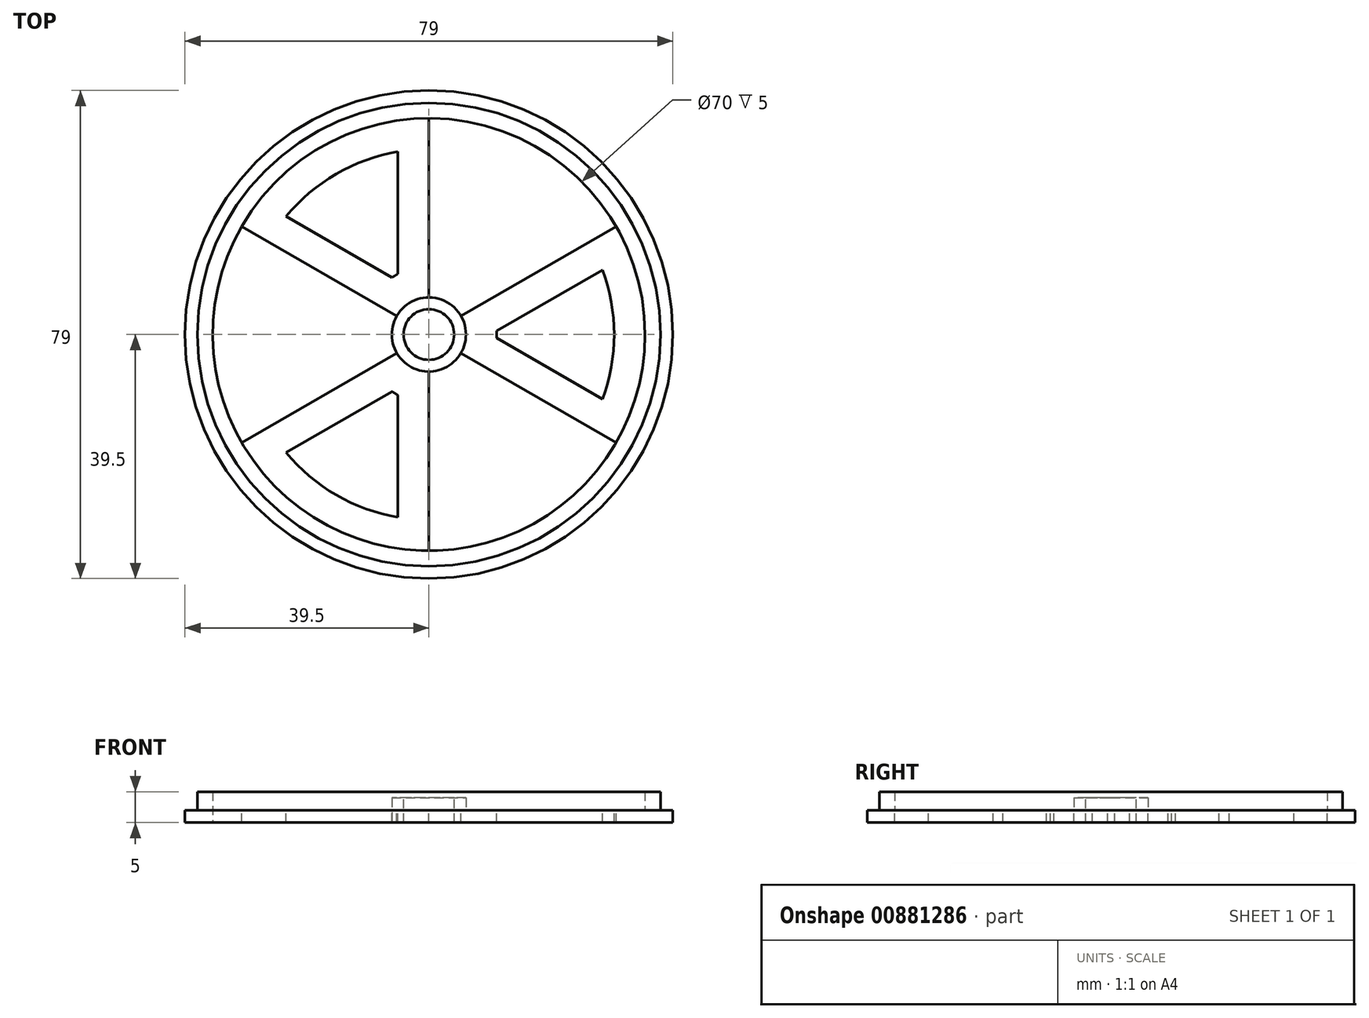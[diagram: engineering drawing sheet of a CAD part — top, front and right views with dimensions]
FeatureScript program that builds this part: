
annotation { "Feature Type Name" : "Feature", "Feature Type Description" : "" }
export const myFeature = defineFeature(function(context is Context, id is Id, definition is map)
    precondition{}
    {
        {
            var Q0;
            Q0=qCreatedBy(makeId("Top.planeOp"),FACE);
            var sketch = newSketch(context, id + "F0", { "sketchPlane" : qUnion([Q0])});
            skCircle(sketch, "E0", {"center": v(0, 0) * mm, "radius": 39.5 * mm});
            skSolve(sketch);
        }
        {
            var Q0;
            Q0=makeQuery(id+"F0.imprint","IMPRINT",FACE,{"disambiguationData":[TD([[makeQuery(id+"F0.imprint","IMPRINT",EDGE,{"derivedFrom":sQuery(id+"F0.wireOp",EDGE,"E0")}),1.0]])]});
            extrude(context, id + "F1", {"entities" : qUnion([Q0]), "depth" : 2 * mm, "offsetDistance" : 25 * mm});
        }
        {
            var Q0;
            Q0=makeQuery(id+"F1.opExtrude","CAP_FACE",FACE,{"disambiguationData":[OSD([sQuery(id+"F0.wireOp",EDGE,"E0")])],"isStart":false});
            var sketch = newSketch(context, id + "F2", { "sketchPlane" : qUnion([Q0])});
            skCircle(sketch, "E1", {"center": v(0, 0) * mm, "radius": 37.5 * mm});
            skCircle(sketch, "E2", {"center": v(0, 0) * mm, "radius": 35 * mm});
            skSolve(sketch);
        }
        {
            var Q0;
            Q0=makeQuery(id+"F2.imprint","IMPRINT",FACE,{"disambiguationData":[TD([[makeQuery(id+"F2.imprint","IMPRINT",EDGE,{"derivedFrom":sQuery(id+"F2.wireOp",EDGE,"E1")}),1.0]])]});
            extrude(context, id + "F3", {"entities" : qUnion([Q0]), "operationType" : NewBodyOperationType.ADD, "depth" : 3 * mm, "offsetDistance" : 25 * mm});
        }
        {
            var Q0;
            Q0=makeQuery(id+"F3.boolean.opBoolean","SPLIT",FACE,{"disambiguationData":[TD([makeQuery(id+"F3.opExtrude","SWEPT_FACE",FACE,{"disambiguationData":[OSD([sQuery(id+"F2.wireOp",EDGE,"E2")])]})])],"derivedFrom":makeQuery(id+"F1.opExtrude","CAP_FACE",FACE,{"disambiguationData":[OSD([sQuery(id+"F0.wireOp",EDGE,"E0")])],"isStart":false})});
            var sketch = newSketch(context, id + "F4", { "sketchPlane" : qUnion([Q0])});
            skCircle(sketch, "E3", {"center": v(0, 0) * mm, "radius": 4.1 * mm});
            skSolve(sketch);
        }
        {
            var Q0;
            Q0=makeQuery(id+"F4.imprint","IMPRINT",FACE,{"disambiguationData":[TD([[makeQuery(id+"F4.imprint","IMPRINT",EDGE,{"derivedFrom":sQuery(id+"F4.wireOp",EDGE,"E3")}),1.0]])]});
            extrude(context, id + "F5", {"entities" : qUnion([Q0]), "operationType" : NewBodyOperationType.REMOVE, "oppositeDirection" : true, "depth" : 25 * mm, "offsetDistance" : 25 * mm});
        }
        {
            var Q0;
            Q0=makeQuery(id+"F3.boolean.opBoolean","SPLIT",FACE,{"disambiguationData":[TD([makeQuery(id+"F3.opExtrude","SWEPT_FACE",FACE,{"disambiguationData":[OSD([sQuery(id+"F2.wireOp",EDGE,"E2")])]})])],"derivedFrom":makeQuery(id+"F1.opExtrude","CAP_FACE",FACE,{"disambiguationData":[OSD([sQuery(id+"F0.wireOp",EDGE,"E0")])],"isStart":false})});
            var sketch = newSketch(context, id + "F6", { "sketchPlane" : qUnion([Q0])});
            skCircle(sketch, "E4", {"center": v(0, 0) * mm, "radius": 4.1 * mm});
            skCircle(sketch, "E5", {"center": v(0, 0) * mm, "radius": 6 * mm});
            skSolve(sketch);
        }
        {
            var Q0;
            Q0=makeQuery(id+"F6.imprint","IMPRINT",FACE,{"disambiguationData":[TD([[makeQuery(id+"F6.imprint","IMPRINT",EDGE,{"derivedFrom":sQuery(id+"F6.wireOp",EDGE,"E4")}),-1.0]])]});
            extrude(context, id + "F7", {"entities" : qUnion([Q0]), "operationType" : NewBodyOperationType.ADD, "depth" : 2 * mm, "offsetDistance" : 25 * mm});
        }
        {
            var Q0;
            Q0=makeQuery(id+"F3.boolean.opBoolean","SPLIT",FACE,{"disambiguationData":[TD([makeQuery(id+"F3.opExtrude","SWEPT_FACE",FACE,{"disambiguationData":[OSD([sQuery(id+"F2.wireOp",EDGE,"E2")])]})])],"derivedFrom":makeQuery(id+"F1.opExtrude","CAP_FACE",FACE,{"disambiguationData":[OSD([sQuery(id+"F0.wireOp",EDGE,"E0")])],"isStart":false})});
            var sketch = newSketch(context, id + "F8", { "sketchPlane" : qUnion([Q0])});
            skCircle(sketch, "E6.cCircle", {"center": v(0, 0) * mm, "radius": 35 * mm, "construction": true});
            skLineSegment(sketch, "E6.0", {"start": v(0, 35) * mm, "end": v(30.31, 17.5) * mm});
            skLineSegment(sketch, "E6.1", {"start": v(30.31, 17.5) * mm, "end": v(30.31, -17.5) * mm});
            skLineSegment(sketch, "E6.2", {"start": v(30.31, -17.5) * mm, "end": v(0, -35) * mm});
            skLineSegment(sketch, "E6.3", {"start": v(0, -35) * mm, "end": v(-30.31, -17.5) * mm});
            skLineSegment(sketch, "E6.4", {"start": v(-30.31, -17.5) * mm, "end": v(-30.31, 17.5) * mm});
            skLineSegment(sketch, "E6.5", {"start": v(-30.31, 17.5) * mm, "end": v(0, 35) * mm});
            skCircle(sketch, "E7.cCircle", {"center": v(0, 0) * mm, "radius": 6 * mm, "construction": true});
            skLineSegment(sketch, "E7.0", {"start": v(0, 6) * mm, "end": v(5.2, 3) * mm});
            skLineSegment(sketch, "E7.1", {"start": v(5.2, 3) * mm, "end": v(5.2, -3) * mm});
            skLineSegment(sketch, "E7.2", {"start": v(5.2, -3) * mm, "end": v(0, -6) * mm});
            skLineSegment(sketch, "E7.3", {"start": v(0, -6) * mm, "end": v(-5.2, -3) * mm});
            skLineSegment(sketch, "E7.4", {"start": v(-5.2, -3) * mm, "end": v(-5.2, 3) * mm});
            skLineSegment(sketch, "E7.5", {"start": v(-5.2, 3) * mm, "end": v(0, 6) * mm});
            skLineSegment(sketch, "E8", {"start": v(0, 35) * mm, "end": v(0, 6) * mm});
            skLineSegment(sketch, "E9", {"start": v(30.31, 17.5) * mm, "end": v(5.2, 3) * mm});
            skLineSegment(sketch, "E10", {"start": v(30.31, -17.5) * mm, "end": v(5.2, -3) * mm});
            skLineSegment(sketch, "E11", {"start": v(0, -35) * mm, "end": v(0, -6) * mm});
            skLineSegment(sketch, "E12", {"start": v(-30.31, -17.5) * mm, "end": v(-5.2, -3) * mm});
            skLineSegment(sketch, "E13", {"start": v(-30.31, 17.5) * mm, "end": v(-5.2, 3) * mm});
            skSolve(sketch);
        }
        {
            var Q0;
            Q0=makeQuery(id+"F8.imprint","IMPRINT",FACE,{"disambiguationData":[TD([[makeQuery(id+"F8.imprint","IMPRINT",EDGE,{"derivedFrom":sQuery(id+"F8.wireOp",EDGE,"E6.0")}),-1.0]])]});
            var Q1;
            Q1=makeQuery(id+"F8.imprint","IMPRINT",FACE,{"disambiguationData":[TD([[makeQuery(id+"F8.imprint","IMPRINT",EDGE,{"derivedFrom":sQuery(id+"F8.wireOp",EDGE,"E6.2")}),-1.0]])]});
            var Q2;
            {var subQ0=sQuery(id+"F8.wireOp",EDGE,"E6.0");Q2=makeQuery(id+"F8.imprint","IMPRINT",FACE,{"disambiguationData":[TD([[makeQuery(id+"F8.imprint","IMPRINT",EDGE,{"derivedFrom":subQ0}),1.0]])]});}
            var Q3;
            {var subQ0=sQuery(id+"F8.wireOp",EDGE,"E6.2");Q3=makeQuery(id+"F8.imprint","IMPRINT",FACE,{"disambiguationData":[TD([[makeQuery(id+"F8.imprint","IMPRINT",EDGE,{"derivedFrom":subQ0}),1.0]])]});}
            var Q4;
            Q4=makeQuery(id+"F8.imprint","IMPRINT",FACE,{"disambiguationData":[TD([[makeQuery(id+"F8.imprint","IMPRINT",EDGE,{"derivedFrom":sQuery(id+"F8.wireOp",EDGE,"E6.4")}),-1.0]])]});
            var Q5;
            {var subQ0=sQuery(id+"F8.wireOp",EDGE,"E6.4");Q5=makeQuery(id+"F8.imprint","IMPRINT",FACE,{"disambiguationData":[TD([[makeQuery(id+"F8.imprint","IMPRINT",EDGE,{"derivedFrom":subQ0}),1.0]])]});}
            extrude(context, id + "F9", {"entities" : qUnion([Q0, Q1, Q2, Q3, Q4, Q5]), "operationType" : NewBodyOperationType.REMOVE, "oppositeDirection" : true, "depth" : 25 * mm, "offsetDistance" : 25 * mm});
        }
        {
            var Q0;
            {var subQ0=sQuery(id+"F8.wireOp",EDGE,"E9");var subQ4=sQuery(id+"F2.wireOp",EDGE,"E2");var subQ15=makeQuery(id+"F3.opExtrude","SWEPT_FACE",FACE,{"disambiguationData":[OSD([subQ4])]});Q0=makeQuery(id+"F9.boolean.opBoolean","SPLIT",FACE,{"disambiguationData":[TD([makeQuery(id+"F9.opExtrude","SWEPT_FACE",FACE,{"disambiguationData":[OSD([subQ0])]})])],"derivedFrom":makeQuery(id+"F3.boolean.opBoolean","SPLIT",FACE,{"disambiguationData":[TD([subQ15])],"derivedFrom":makeQuery(id+"F1.opExtrude","CAP_FACE",FACE,{"disambiguationData":[OSD([sQuery(id+"F0.wireOp",EDGE,"E0")])],"isStart":false})})});}
            var sketch = newSketch(context, id + "F10", { "sketchPlane" : qUnion([Q0])});
            skLineSegment(sketch, "E14.0", {"start": v(10.99, -0.57) * mm, "end": v(28.12, -10.46) * mm});
            skArc(sketch, "E14.1", {"start": v(10.99, 0.57) * mm, "mid": v(11, 0) * mm, "end": v(10.99, -0.57) * mm});
            skLineSegment(sketch, "E14.2", {"start": v(28.12, 10.46) * mm, "end": v(10.99, 0.57) * mm});
            skArc(sketch, "E14.3", {"start": v(28.12, -10.46) * mm, "mid": v(30, 0) * mm, "end": v(28.12, 10.46) * mm});
            skArc(sketch, "E15.0", {"start": v(-5, 29.58) * mm, "mid": v(-15, 25.98) * mm, "end": v(-23.12, 19.12) * mm});
            skLineSegment(sketch, "E15.1", {"start": v(-5, 9.8) * mm, "end": v(-5, 29.58) * mm});
            skArc(sketch, "E15.2", {"start": v(-5.99, 9.23) * mm, "mid": v(-5.5, 9.53) * mm, "end": v(-5, 9.8) * mm});
            skLineSegment(sketch, "E15.3", {"start": v(-23.12, 19.12) * mm, "end": v(-5.99, 9.23) * mm});
            skLineSegment(sketch, "E16.0", {"start": v(-5.99, -9.23) * mm, "end": v(-23.12, -19.12) * mm});
            skArc(sketch, "E16.1", {"start": v(-5, -9.8) * mm, "mid": v(-5.5, -9.53) * mm, "end": v(-5.99, -9.23) * mm});
            skLineSegment(sketch, "E16.2", {"start": v(-5, -29.58) * mm, "end": v(-5, -9.8) * mm});
            skArc(sketch, "E16.3", {"start": v(-23.12, -19.12) * mm, "mid": v(-15, -25.98) * mm, "end": v(-5, -29.58) * mm});
            skSolve(sketch);
        }
        {
            var Q0;
            Q0=makeQuery(id+"F10.imprint","IMPRINT",FACE,{"disambiguationData":[TD([[makeQuery(id+"F10.imprint","IMPRINT",EDGE,{"derivedFrom":sQuery(id+"F10.wireOp",EDGE,"E15.0")}),1.0]])]});
            var Q1;
            Q1=makeQuery(id+"F10.imprint","IMPRINT",FACE,{"disambiguationData":[TD([[makeQuery(id+"F10.imprint","IMPRINT",EDGE,{"derivedFrom":sQuery(id+"F10.wireOp",EDGE,"E14.0")}),1.0]])]});
            var Q2;
            Q2=makeQuery(id+"F10.imprint","IMPRINT",FACE,{"disambiguationData":[TD([[makeQuery(id+"F10.imprint","IMPRINT",EDGE,{"derivedFrom":sQuery(id+"F10.wireOp",EDGE,"E16.0")}),1.0]])]});
            extrude(context, id + "F11", {"entities" : qUnion([Q0, Q1, Q2]), "operationType" : NewBodyOperationType.REMOVE, "oppositeDirection" : true, "depth" : 25 * mm, "offsetDistance" : 25 * mm});
        }
    });
